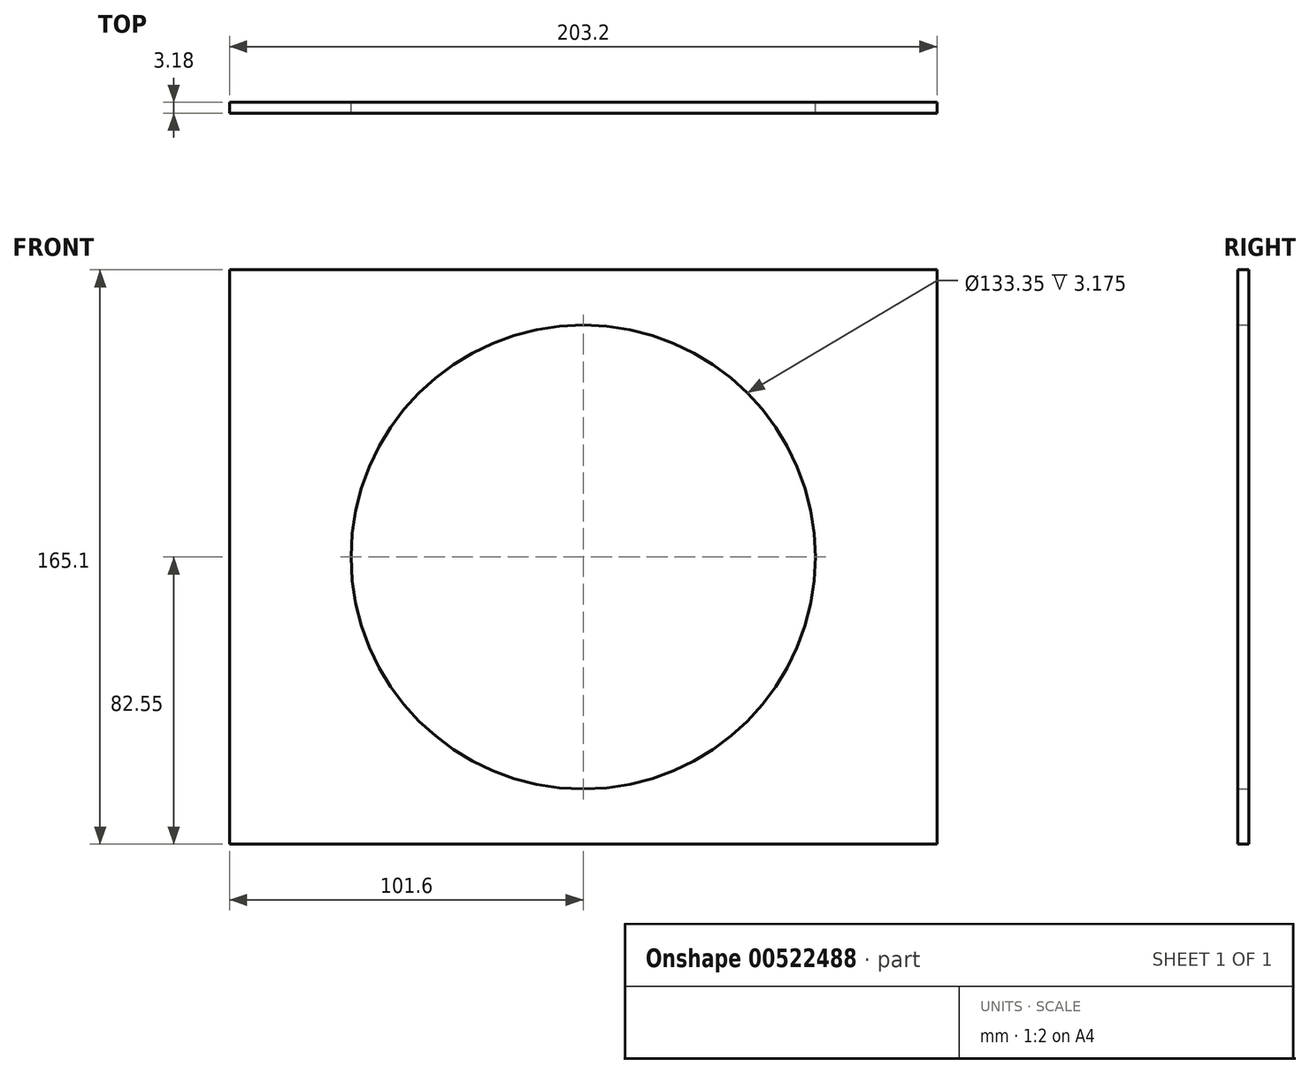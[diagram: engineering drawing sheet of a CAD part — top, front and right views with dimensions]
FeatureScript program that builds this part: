
annotation { "Feature Type Name" : "Feature", "Feature Type Description" : "" }
export const myFeature = defineFeature(function(context is Context, id is Id, definition is map)
    precondition{}
    {
        {
            var Q0;
            Q0=qCreatedBy(makeId("Front.planeOp"),FACE);
            var sketch = newSketch(context, id + "F0", { "sketchPlane" : qUnion([Q0])});
            skLineSegment(sketch, "E0.bottom", {"start": v(-101.6, 82.55) * mm, "end": v(101.6, 82.55) * mm});
            skLineSegment(sketch, "E0.top", {"start": v(-101.6, -82.55) * mm, "end": v(101.6, -82.55) * mm});
            skLineSegment(sketch, "E0.left", {"start": v(-101.6, 82.55) * mm, "end": v(-101.6, -82.55) * mm});
            skLineSegment(sketch, "E0.right", {"start": v(101.6, 82.55) * mm, "end": v(101.6, -82.55) * mm});
            skPoint(sketch, "E0.middle", {"position": v(0, 0) * mm});
            skSolve(sketch);
        }
        {
            var Q0;
            Q0=makeQuery(id+"F0.imprint","IMPRINT",FACE,{"disambiguationData":[TD([[makeQuery(id+"F0.imprint","IMPRINT",EDGE,{"derivedFrom":sQuery(id+"F0.wireOp",EDGE,"E0.bottom")}),-1.0]])]});
            extrude(context, id + "F1", {"entities" : qUnion([Q0]), "depth" : 3.17 * mm, "offsetDistance" : 25.4 * mm});
        }
        {
            var Q0;
            Q0=makeQuery(id+"F1.opExtrude","CAP_FACE",FACE,{"disambiguationData":[OSD([sQuery(id+"F0.wireOp",EDGE,"E0.bottom"),sQuery(id+"F0.wireOp",EDGE,"E0.top"),sQuery(id+"F0.wireOp",EDGE,"E0.left"),sQuery(id+"F0.wireOp",EDGE,"E0.right")])],"isStart":false});
            var sketch = newSketch(context, id + "F2", { "sketchPlane" : qUnion([Q0])});
            skCircle(sketch, "E1", {"center": v(0, 0) * mm, "radius": 66.68 * mm});
            skSolve(sketch);
        }
        {
            var Q0;
            Q0=makeQuery(id+"F2.imprint","IMPRINT",FACE,{"disambiguationData":[TD([[makeQuery(id+"F2.imprint","IMPRINT",EDGE,{"derivedFrom":sQuery(id+"F2.wireOp",EDGE,"E1")}),1.0]])]});
            extrude(context, id + "F3", {"entities" : qUnion([Q0]), "operationType" : NewBodyOperationType.REMOVE, "endBound" : BoundingType.SYMMETRIC, "depth" : 25.4 * mm, "offsetDistance" : 25.4 * mm});
        }
    });
